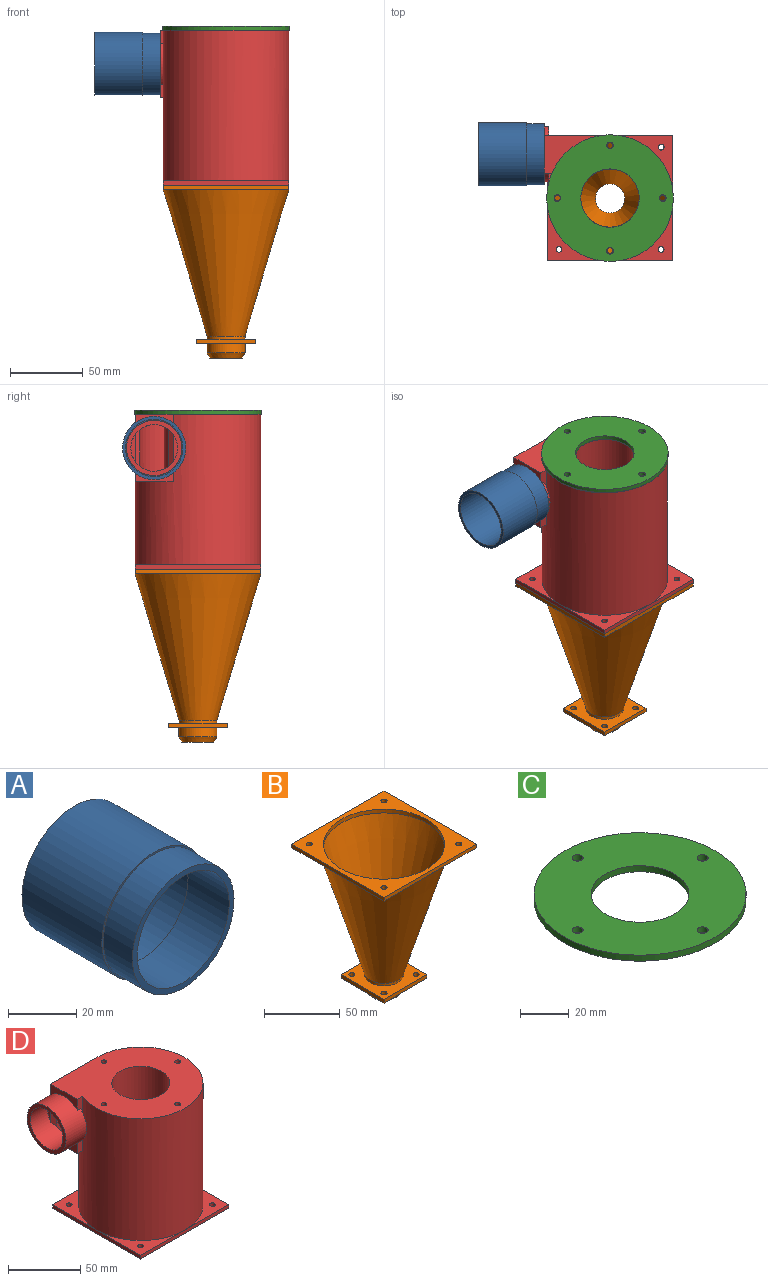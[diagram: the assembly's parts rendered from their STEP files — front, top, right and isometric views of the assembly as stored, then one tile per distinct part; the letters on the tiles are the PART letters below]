
ASSEMBLY  parts=4 mates=5
PART A: 8 faces, bbox 43.3x45x43.3 mm
  f0: plane 39.3x39.3mm, normal (0,1,0), area 78.9mm2, adj f2,f4
  f1: cylinder r=21mm len=42mm, axis (0,1,0), area 1583.4mm2, adj f3,f7
  f2: cylinder r=19mm len=38mm, axis (0,1,0), area 2029.5mm2, adj f0,f3
  f3: plane 42x42mm, normal (0,-1,0), area 251.3mm2, adj f1,f2
  f4: cylinder r=19.65mm len=39.3mm, axis (0,-1,0), area 3457mm2, adj f0,f6
  f5: cylinder r=21.65mm len=43.3mm, axis (0,-1,0), area 4489mm2, adj f6,f7
  f6: plane 43.3x43.3mm, normal (0,1,0), area 259.5mm2, adj f4,f5
  f7: plane 43.3x43.3mm, normal (0,-1,0), area 87.1mm2, adj f1,f5
PART B: 35 faces, bbox 86.3x86.3x118.4 mm
  f0: cylinder r=13mm len=26mm, axis (0,0,1), area 163.4mm2, adj f8,f28
  f1: plane 6.75x0.13mm, normal (0,0,1), area 0.6mm2, adj f8,f15
  f2: plane 6.75x0.13mm, normal (0,0,1), area 0.6mm2, adj f8,f18
  f3: plane 6.75x0.13mm, normal (0,0,1), area 0.6mm2, adj f8,f17
  f4: plane 22x22mm, normal (0,0,-1), area 66mm2, adj f5,f34
  f5: cylinder r=10mm len=20mm, axis (0,0,1), area 970.1mm2, adj f4,f6
  f6: cone r=10mm half-angle=16.7deg, axis (0,0,1), area 16399.6mm2, adj f5,f23
  f7: plane 6.75x0.13mm, normal (0,0,1), area 0.6mm2, adj f8,f16
  f8: cone r=43.13mm half-angle=16.7deg, axis (0,0,1), area 18491.9mm2, adj f0,f1,f2,f3,f7,f10,f11,f12
  f9: cylinder r=13mm len=26mm, axis (0,0,1), area 533.9mm2, adj f29,f34
  f10: plane 39.63x39.63mm, normal (0,0,-1), area 375.9mm2, adj f8,f16,f17,f21
  f11: plane 39.63x39.63mm, normal (0,0,-1), area 375.9mm2, adj f8,f17,f18,f20
  f12: plane 39.63x39.63mm, normal (0,0,-1), area 375.9mm2, adj f8,f15,f18,f19
  f13: plane 39.63x39.63mm, normal (0,0,-1), area 375.9mm2, adj f8,f15,f16,f22
  f14: plane 86x86mm, normal (0,0,1), area 2319.2mm2, adj f15,f16,f17,f18,f19,f20,f21,f22
  f15: plane 86x3mm, normal (-1,0,0), area 258mm2, adj f1,f12,f13,f14,f16,f18
  f16: plane 86x3mm, normal (0,-1,0), area 258mm2, adj f7,f10,f13,f14,f15,f17
  f17: plane 86x3mm, normal (1,0,0), area 258mm2, adj f3,f10,f11,f14,f16,f18
  f18: plane 86x3mm, normal (0,1,0), area 258mm2, adj f2,f11,f12,f14,f15,f17
  f19: cylinder r=2mm len=4mm, axis (0,0,-1), area 37.7mm2, adj f12,f14
  f20: cylinder r=2mm len=4mm, axis (0,0,-1), area 37.7mm2, adj f11,f14
  f21: cylinder r=2mm len=4mm, axis (0,0,-1), area 37.7mm2, adj f10,f14
  f22: cylinder r=2mm len=4mm, axis (0,0,-1), area 37.7mm2, adj f13,f14
  f23: cylinder r=40mm len=80mm, axis (0,0,-1), area 754mm2, adj f6,f14
  f24: plane 40x3mm, normal (-1,0,0), area 120mm2, adj f25,f27,f28,f29
  f25: plane 40x3mm, normal (0,-1,0), area 120mm2, adj f24,f26,f28,f29
  f26: plane 40x3mm, normal (1,0,0), area 120mm2, adj f25,f27,f28,f29
  f27: plane 40x3mm, normal (0,1,0), area 120mm2, adj f24,f26,f28,f29
  f28: plane 40x40mm, normal (0,0,1), area 1018.8mm2, adj f0,f24,f25,f26,f27,f30,f31,f32
  f29: plane 40x40mm, normal (0,0,-1), area 1018.8mm2, adj f9,f24,f25,f26,f27,f30,f31,f32
  f30: cylinder r=2mm len=4mm, axis (0,0,-1), area 37.7mm2, adj f28,f29
  f31: cylinder r=2mm len=4mm, axis (0,0,-1), area 37.7mm2, adj f28,f29
  f32: cylinder r=2mm len=4mm, axis (0,0,-1), area 37.7mm2, adj f28,f29
  f33: cylinder r=2mm len=4mm, axis (0,0,-1), area 37.7mm2, adj f28,f29
  f34: cone r=13mm half-angle=30deg, axis (0,0,1), area 301.6mm2, adj f4,f9
PART C: 8 faces, bbox 86.7x86.7x3 mm
  f0: plane 86.71x86.71mm, normal (0,0,1), area 4584.9mm2, adj f1,f2,f3,f4,f6,f7
  f1: cylinder r=43.35mm len=86.71mm, axis (0,0,-1), area 817.2mm2, adj f0,f5
  f2: cylinder r=2.25mm len=4.5mm, axis (0,0,-1), area 42.4mm2, adj f0,f5
  f3: cylinder r=2.25mm len=4.5mm, axis (0,0,-1), area 42.4mm2, adj f0,f5
  f4: cylinder r=2.25mm len=4.5mm, axis (0,0,-1), area 42.4mm2, adj f0,f5
  f5: plane 86.71x86.71mm, normal (0,0,-1), area 4584.9mm2, adj f1,f2,f3,f4,f6,f7
  f6: cylinder r=20mm len=40mm, axis (0,0,-1), area 377mm2, adj f0,f5
  f7: cylinder r=2.25mm len=4.5mm, axis (0,0,-1), area 42.4mm2, adj f0,f5
PART D: 46 faces, bbox 105x92x106 mm
  f0: cylinder r=16mm len=32mm, axis (-1,0,0), area 1863.6mm2, adj f1,f36,f38,f42,f43,f44,f45
  f1: plane 20x7.51mm, normal (1,0,0), area 102.3mm2, adj f0,f6,f29,f31
  f2: cylinder r=19mm len=38mm, axis (1,0,0), area 2215.8mm2, adj f24,f26,f37,f38,f39,f40,f41
  f3: plane 43x23.59mm, normal (0.7,-0.72,0), area 270.7mm2, adj f5,f6,f27,f28,f29,f30
  f4: cylinder r=23mm len=80mm, axis (0,0,1), area 11561.1mm2, adj f6,f7
  f5: cylinder r=40mm len=103mm, axis (0,0,1), area 23940mm2, adj f3,f6,f14,f27,f28,f31
  f6: plane 82x80mm, normal (0,0,-1), area 3622.8mm2, adj f1,f3,f4,f5,f28,f29,f31,f32
  f7: plane 46x46mm, normal (0,0,-1), area 405.3mm2, adj f4,f8
  f8: cylinder r=20mm len=83mm, axis (0,0,1), area 10430.1mm2, adj f7,f9
  f9: plane 88x86mm, normal (0,0,1), area 4931.2mm2, adj f8,f10,f24,f26,f32,f33,f34,f35
  f10: cylinder r=43mm len=103mm, axis (0,0,1), area 25525.1mm2, adj f9,f11,f12,f13,f15,f24,f25,f26
  f11: plane 43x43mm, normal (0,0,1), area 384.2mm2, adj f10,f18,f19,f21
  f12: plane 43x43mm, normal (0,0,1), area 384.2mm2, adj f10,f17,f18,f22
  f13: plane 43x43mm, normal (0,0,1), area 384.2mm2, adj f10,f16,f17,f23
  f14: plane 86x86mm, normal (0,0,-1), area 2319.2mm2, adj f5,f16,f17,f18,f19,f20,f21,f22
  f15: plane 43x43mm, normal (0,0,1), area 384.2mm2, adj f10,f16,f19,f20
  f16: plane 86x3mm, normal (-1,0,0), area 258mm2, adj f13,f14,f15,f17,f19
  f17: plane 86x3mm, normal (0,1,0), area 258mm2, adj f12,f13,f14,f16,f18
  f18: plane 86x3mm, normal (1,0,0), area 258mm2, adj f11,f12,f14,f17,f19
  f19: plane 86x3mm, normal (0,-1,0), area 258mm2, adj f11,f14,f15,f16,f18
  f20: cylinder r=2mm len=4mm, axis (0,0,1), area 37.7mm2, adj f14,f15
  f21: cylinder r=2mm len=4mm, axis (0,0,1), area 37.7mm2, adj f11,f14
  f22: cylinder r=2mm len=4mm, axis (0,0,1), area 37.7mm2, adj f12,f14
  f23: cylinder r=2mm len=4mm, axis (0,0,1), area 37.7mm2, adj f13,f14
  f24: plane 46x5.5mm, normal (0,-1,0), area 170mm2, adj f2,f9,f10,f25,f37,f40,f41
  f25: plane 45x26mm, normal (0,0,-1), area 429.3mm2, adj f10,f24,f26,f41
  f26: plane 46x45mm, normal (0,1,0), area 1986.9mm2, adj f2,f9,f10,f25,f39,f40,f41
  f27: plane 36.21x23mm, normal (0,0,-1), area 326.4mm2, adj f3,f5,f28
  f28: plane 43x12.62mm, normal (0,-1,0), area 542.6mm2, adj f3,f5,f6,f27
  f29: plane 40x21.49mm, normal (0,1,0), area 859.5mm2, adj f1,f3,f6,f30,f36,f45
  f30: plane 42x20mm, normal (0,0,1), area 634.9mm2, adj f3,f29,f31,f36
  f31: plane 42x40mm, normal (0,-1,0), area 1680mm2, adj f1,f5,f6,f30,f36,f44
  f32: cylinder r=2mm len=4mm, axis (0,0,1), area 37.7mm2, adj f6,f9
  f33: cylinder r=2mm len=4mm, axis (0,0,1), area 37.7mm2, adj f6,f9
  f34: cylinder r=2mm len=4mm, axis (0,0,1), area 37.7mm2, adj f6,f9
  f35: cylinder r=2mm len=4mm, axis (0,0,1), area 37.7mm2, adj f6,f9
  f36: plane 20x7.51mm, normal (1,0,0), area 102.3mm2, adj f0,f29,f30,f31
  f37: plane 27.71x6mm, normal (1,0,0), area 114.9mm2, adj f2,f24
  f38: plane 38x38mm, normal (-1,0,0), area 329.9mm2, adj f0,f2
  f39: plane 27.71x6mm, normal (1,0,0), area 114.9mm2, adj f2,f26
  f40: plane 26x9.14mm, normal (-1,0,0), area 145.8mm2, adj f2,f9,f24,f26
  f41: plane 26x9.14mm, normal (-1,0,0), area 145.8mm2, adj f2,f24,f25,f26
  f42: plane 18.65x3mm, normal (-1,0,0), area 38.1mm2, adj f0,f44
  f43: plane 18.65x3mm, normal (-1,0,0), area 38.1mm2, adj f0,f45
  f44: plane 24.98x3mm, normal (-0.71,-0.71,0), area 93.8mm2, adj f0,f31,f42
  f45: plane 24.98x3mm, normal (-0.71,0.71,0), area 93.8mm2, adj f0,f29,f43
PLACE A rot(axis=(0.71,-0.71,0),180deg) t=(-27.9,-73.31,203.64)mm
PLACE B t=(29.1,-103.31,2.2)mm
PLACE C t=(29.1,-103.43,226.64)mm
PLACE D t=(29.1,-103.31,123.64)mm
MATE cylindrical B.f0 <-> D.f4  axis (0,0,-1) through (29.1,-103.31,119.14)mm
MATE fastened D.f4 <-> B.f0  axis (0,0,-1) through (29.1,-103.31,120.64)mm
MATE fastened C.f2 <-> D.f32  axis (0,0,-1) through (29.1,-67.31,226.64)mm
MATE fastened A.f5 <-> D.f0  axis (-1,0,0) through (-32.9,-73.31,203.64)mm
MATE slider A.f2 <-> D.f0  axis (-1,0,0) through (-15.9,-73.31,203.64)mm
